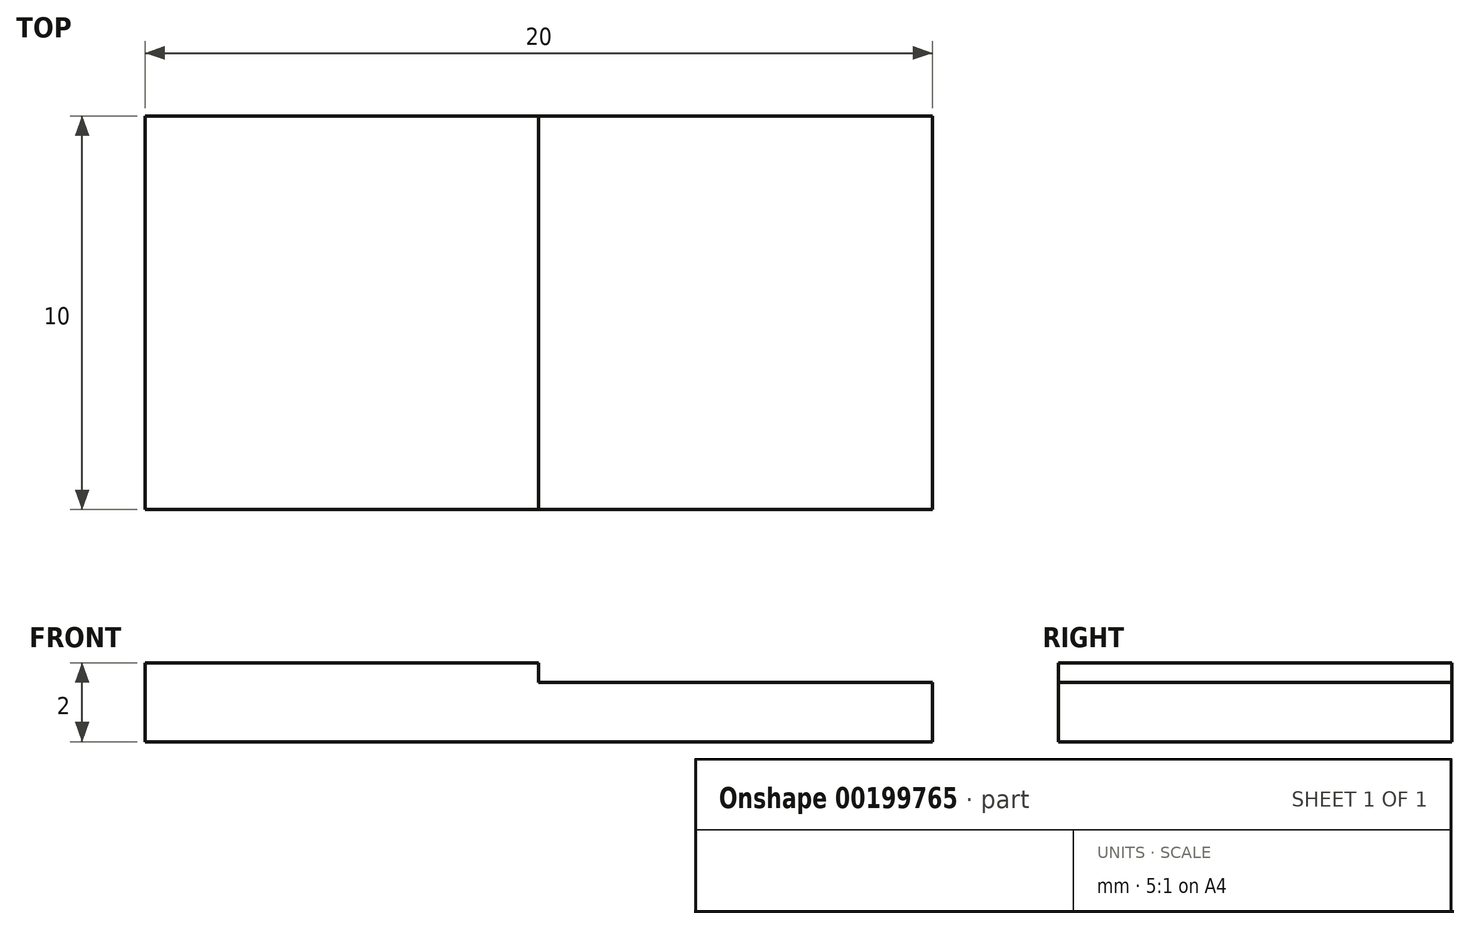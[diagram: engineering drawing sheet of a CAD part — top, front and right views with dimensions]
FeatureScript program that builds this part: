
annotation { "Feature Type Name" : "Feature", "Feature Type Description" : "" }
export const myFeature = defineFeature(function(context is Context, id is Id, definition is map)
    precondition{}
    {
        {
            var Q0;
            Q0=qCreatedBy(makeId("Top.planeOp"),FACE);
            var sketch = newSketch(context, id + "F0", { "sketchPlane" : qUnion([Q0])});
            skLineSegment(sketch, "E0.bottom", {"start": v(0, 0) * mm, "end": v(10, 0) * mm});
            skLineSegment(sketch, "E0.top", {"start": v(0, 10) * mm, "end": v(10, 10) * mm});
            skLineSegment(sketch, "E0.left", {"start": v(0, 0) * mm, "end": v(0, 10) * mm});
            skLineSegment(sketch, "E0.right", {"start": v(10, 0) * mm, "end": v(10, 10) * mm});
            skSolve(sketch);
        }
        {
            var Q0;
            Q0=makeQuery(id+"F0.imprint","IMPRINT",FACE,{"disambiguationData":[TD([[makeQuery(id+"F0.imprint","IMPRINT",EDGE,{"derivedFrom":sQuery(id+"F0.wireOp",EDGE,"E0.bottom")}),1.0]])]});
            extrude(context, id + "F1", {"entities" : qUnion([Q0]), "depth" : 2 * mm});
        }
        {
            var Q0;
            Q0=qCreatedBy(makeId("Top.planeOp"),FACE);
            var sketch = newSketch(context, id + "F2", { "sketchPlane" : qUnion([Q0])});
            skLineSegment(sketch, "E1.0.0", {"start": v(10, 10) * mm, "end": v(0, 10) * mm});
            skLineSegment(sketch, "E1.0.1", {"start": v(0, 10) * mm, "end": v(0, 0) * mm});
            skLineSegment(sketch, "E1.0.2", {"start": v(0, 0) * mm, "end": v(10, 0) * mm});
            skLineSegment(sketch, "E1.0.3", {"start": v(10, 0) * mm, "end": v(10, 10) * mm});
            skLineSegment(sketch, "E2.bottom", {"start": v(10, 0) * mm, "end": v(20, 0) * mm});
            skLineSegment(sketch, "E2.top", {"start": v(10, 10) * mm, "end": v(20, 10) * mm});
            skLineSegment(sketch, "E2.right", {"start": v(20, 0) * mm, "end": v(20, 10) * mm});
            skSolve(sketch);
        }
        {
            var Q0;
            Q0=makeQuery(id+"F2.imprint","IMPRINT",FACE,{"disambiguationData":[TD([[makeQuery(id+"F2.imprint","IMPRINT",EDGE,{"derivedFrom":sQuery(id+"F2.wireOp",EDGE,"E2.bottom")}),1.0]])]});
            extrude(context, id + "F3", {"entities" : qUnion([Q0]), "operationType" : NewBodyOperationType.ADD, "depth" : 1.5 * mm});
        }
    });
